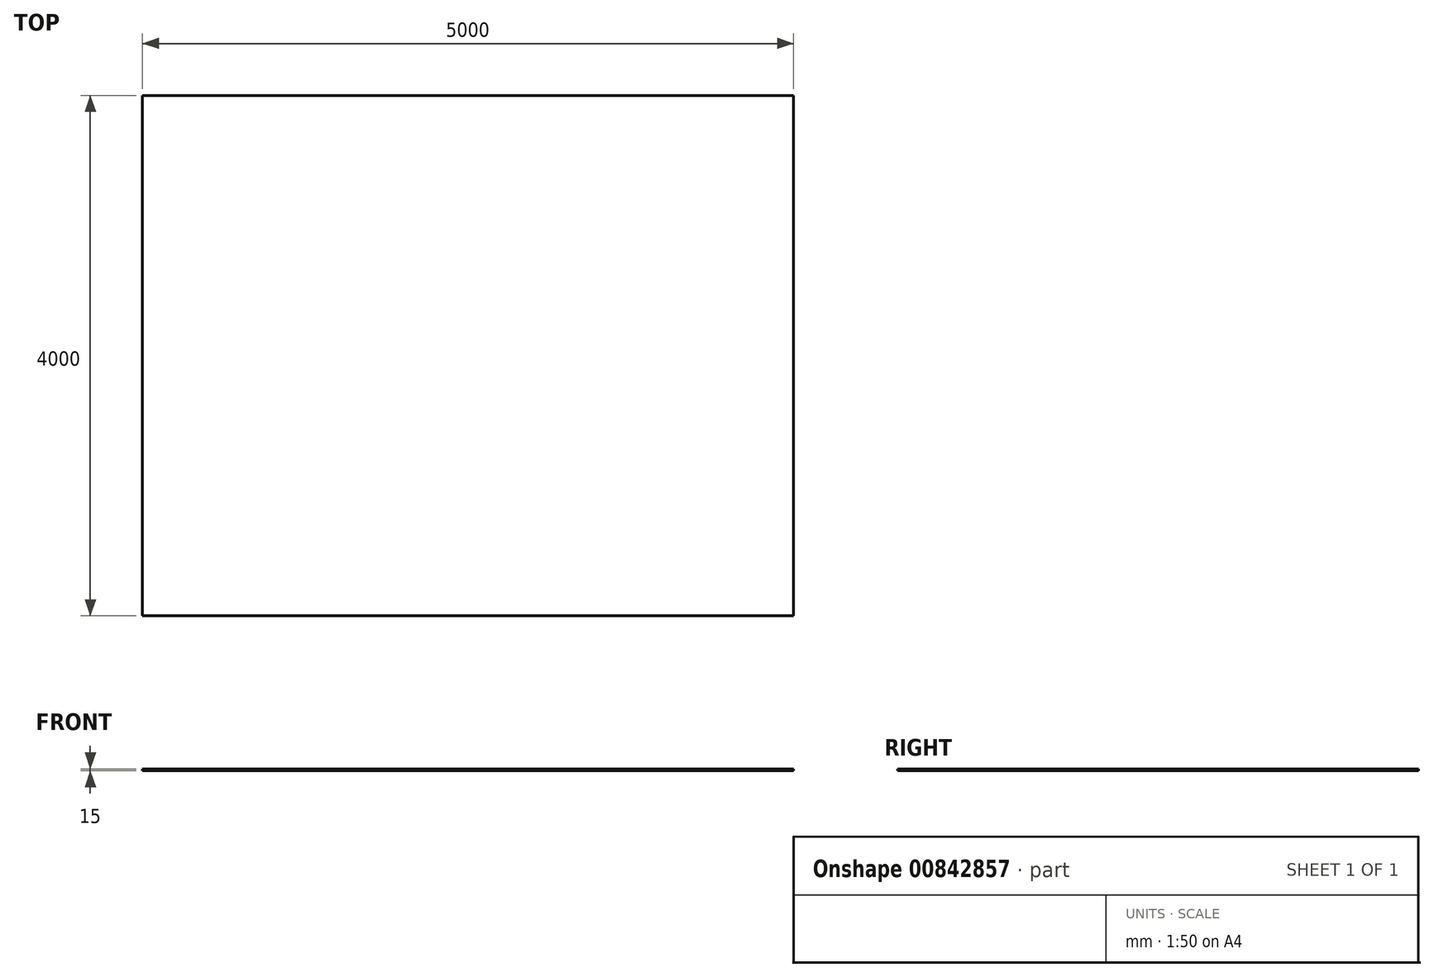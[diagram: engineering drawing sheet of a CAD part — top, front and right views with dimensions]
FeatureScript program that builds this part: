
annotation { "Feature Type Name" : "Feature", "Feature Type Description" : "" }
export const myFeature = defineFeature(function(context is Context, id is Id, definition is map)
    precondition{}
    {
        {
            var Q0;
            Q0=qCreatedBy(makeId("Top.planeOp"),FACE);
            var sketch = newSketch(context, id + "F0", { "sketchPlane" : qUnion([Q0])});
            skLineSegment(sketch, "E0.bottom", {"start": v(-4700.22, 0) * mm, "end": v(299.78, 0) * mm});
            skLineSegment(sketch, "E0.top", {"start": v(-4700.22, -4000) * mm, "end": v(299.78, -4000) * mm});
            skLineSegment(sketch, "E0.left", {"start": v(-4700.22, 0) * mm, "end": v(-4700.22, -4000) * mm});
            skLineSegment(sketch, "E0.right", {"start": v(299.78, 0) * mm, "end": v(299.78, -4000) * mm});
            skSolve(sketch);
        }
        {
            var Q0;
            Q0=makeQuery(id+"F0.imprint","IMPRINT",FACE,{"disambiguationData":[TD([[makeQuery(id+"F0.imprint","IMPRINT",EDGE,{"derivedFrom":sQuery(id+"F0.wireOp",EDGE,"E0.bottom")}),-1.0]])]});
            extrude(context, id + "F1", {"entities" : qUnion([Q0]), "depth" : 15 * mm, "offsetDistance" : 25 * mm});
        }
    });
